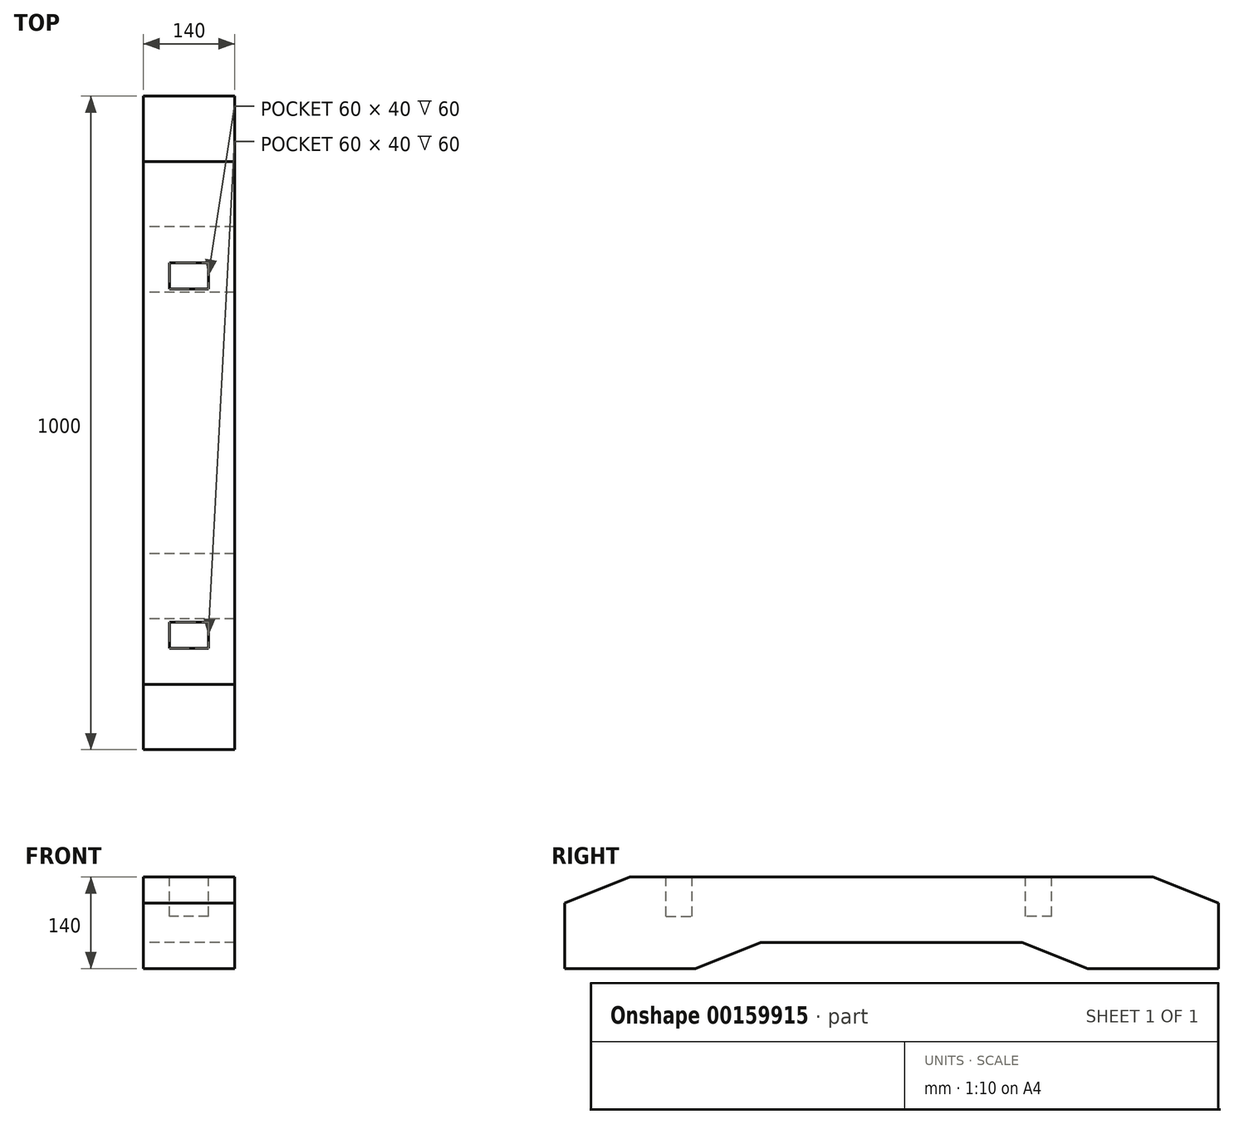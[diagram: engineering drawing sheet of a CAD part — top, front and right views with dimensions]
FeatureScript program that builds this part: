
annotation { "Feature Type Name" : "Feature", "Feature Type Description" : "" }
export const myFeature = defineFeature(function(context is Context, id is Id, definition is map)
    precondition{}
    {
        {
            assignVariable(context, id + "F0", {"name" : "L", "anyValue" : 1000 * mm});
        }
        {
            assignVariable(context, id + "F1", {"name" : "B", "anyValue" : 140 * mm});
        }
        {
            var Q0;
            Q0=qCreatedBy(makeId("Front.planeOp"),FACE);
            var sketch = newSketch(context, id + "F2", { "sketchPlane" : qUnion([Q0])});
            skLineSegment(sketch, "E0.bottom", {"start": v(70, -70) * mm, "end": v(-70, -70) * mm});
            skLineSegment(sketch, "E0.top", {"start": v(70, 70) * mm, "end": v(-70, 70) * mm});
            skLineSegment(sketch, "E0.left", {"start": v(70, -70) * mm, "end": v(70, 70) * mm});
            skLineSegment(sketch, "E0.right", {"start": v(-70, -70) * mm, "end": v(-70, 70) * mm});
            skPoint(sketch, "E0.middle", {"position": v(0, 0) * mm});
            skSolve(sketch);
        }
        {
            var Q0;
            Q0 = qSketchRegion(id + "F2", true);
            extrude(context, id + "F3", {"entities" : qUnion([Q0]), "endBound" : BoundingType.SYMMETRIC, "depth" : getVariable(context, 'L')});
        }
        {
            var Q0;
            Q0=makeQuery(id+"F3.opExtrude","CAP_EDGE",EDGE,{"disambiguationData":[OSD([sQuery(id+"F2.wireOp",EDGE,"E0.top")])],"isStart":false});
            var Q1;
            Q1=makeQuery(id+"F3.opExtrude","CAP_EDGE",EDGE,{"disambiguationData":[OSD([sQuery(id+"F2.wireOp",EDGE,"E0.top")])],"isStart":true});
            chamfer(context, id + "F4", {"entities" : qUnion([Q0, Q1]), "chamferType" : ChamferType.TWO_OFFSETS, "width1" : 40 * mm, "oppositeDirection" : false, "width2" : 100 * mm, "tangentPropagation" : true});
        }
        {
            var Q0;
            Q0=qCreatedBy(makeId("Right.planeOp"),FACE);
            var sketch = newSketch(context, id + "F5", { "sketchPlane" : qUnion([Q0])});
            skLineSegment(sketch, "E1", {"start": v(0, -30) * mm, "end": v(-200, -30) * mm});
            skLineSegment(sketch, "E2", {"start": v(-200, -30) * mm, "end": v(-300, -70) * mm});
            skLineSegment(sketch, "E3", {"start": v(-300, -70) * mm, "end": v(0, -70) * mm});
            skLineSegment(sketch, "E4", {"start": v(0, -70) * mm, "end": v(0, -30) * mm, "construction": true});
            skLineSegment(sketch, "E5.MirrorCS", {"start": v(0, -30) * mm, "end": v(200, -30) * mm});
            skLineSegment(sketch, "E6.MirrorCS", {"start": v(200, -30) * mm, "end": v(300, -70) * mm});
            skLineSegment(sketch, "E7.MirrorCS", {"start": v(300, -70) * mm, "end": v(0, -70) * mm});
            skSolve(sketch);
        }
        {
            var Q0;
            Q0 = qSketchRegion(id + "F5", true);
            extrude(context, id + "F6", {"entities" : qUnion([Q0]), "operationType" : NewBodyOperationType.REMOVE, "endBound" : BoundingType.SYMMETRIC, "depth" : getVariable(context, 'B')});
        }
        {
            var Q0;
            Q0=makeQuery(id+"F3.opExtrude","SWEPT_FACE",FACE,{"disambiguationData":[OSD([sQuery(id+"F2.wireOp",EDGE,"E0.top")])]});
            var sketch = newSketch(context, id + "F7", { "sketchPlane" : qUnion([Q0])});
            skLineSegment(sketch, "E8.bottom", {"start": v(50, -375) * mm, "end": v(-50, -375) * mm, "construction": true});
            skLineSegment(sketch, "E8.top", {"start": v(50, -275) * mm, "end": v(-50, -275) * mm, "construction": true});
            skLineSegment(sketch, "E8.left", {"start": v(50, -375) * mm, "end": v(50, -275) * mm, "construction": true});
            skLineSegment(sketch, "E8.right", {"start": v(-50, -375) * mm, "end": v(-50, -275) * mm, "construction": true});
            skPoint(sketch, "E8.middle", {"position": v(0, -325) * mm});
            skLineSegment(sketch, "E9", {"start": v(0, -325) * mm, "end": v(0, -400) * mm, "construction": true});
            skLineSegment(sketch, "E10.bottom", {"start": v(30, -345) * mm, "end": v(-30, -345) * mm});
            skLineSegment(sketch, "E10.top", {"start": v(30, -305) * mm, "end": v(-30, -305) * mm});
            skLineSegment(sketch, "E10.left", {"start": v(30, -345) * mm, "end": v(30, -305) * mm});
            skLineSegment(sketch, "E10.right", {"start": v(-30, -345) * mm, "end": v(-30, -305) * mm});
            skLineSegment(sketch, "E11", {"start": v(-189.62, -50) * mm, "end": v(155.45, -50) * mm, "construction": true});
            skLineSegment(sketch, "E12.MirrorCS", {"start": v(50, 175) * mm, "end": v(-50, 175) * mm, "construction": true});
            skLineSegment(sketch, "E13.MirrorCS", {"start": v(-50, 275) * mm, "end": v(-50, 175) * mm, "construction": true});
            skLineSegment(sketch, "E14.MirrorCS", {"start": v(50, 275) * mm, "end": v(-50, 275) * mm, "construction": true});
            skLineSegment(sketch, "E15.MirrorCS", {"start": v(50, 275) * mm, "end": v(50, 175) * mm, "construction": true});
            skLineSegment(sketch, "E16.MirrorCS", {"start": v(30, 245) * mm, "end": v(30, 205) * mm});
            skLineSegment(sketch, "E17.MirrorCS", {"start": v(30, 205) * mm, "end": v(-30, 205) * mm});
            skLineSegment(sketch, "E18.MirrorCS", {"start": v(-30, 245) * mm, "end": v(-30, 205) * mm});
            skLineSegment(sketch, "E19.MirrorCS", {"start": v(30, 245) * mm, "end": v(-30, 245) * mm});
            skSolve(sketch);
        }
        {
            var Q0;
            Q0 = qSketchRegion(id + "F7", true);
            extrude(context, id + "F8", {"entities" : qUnion([Q0]), "operationType" : NewBodyOperationType.REMOVE, "oppositeDirection" : true, "depth" : 60 * mm});
        }
    });
